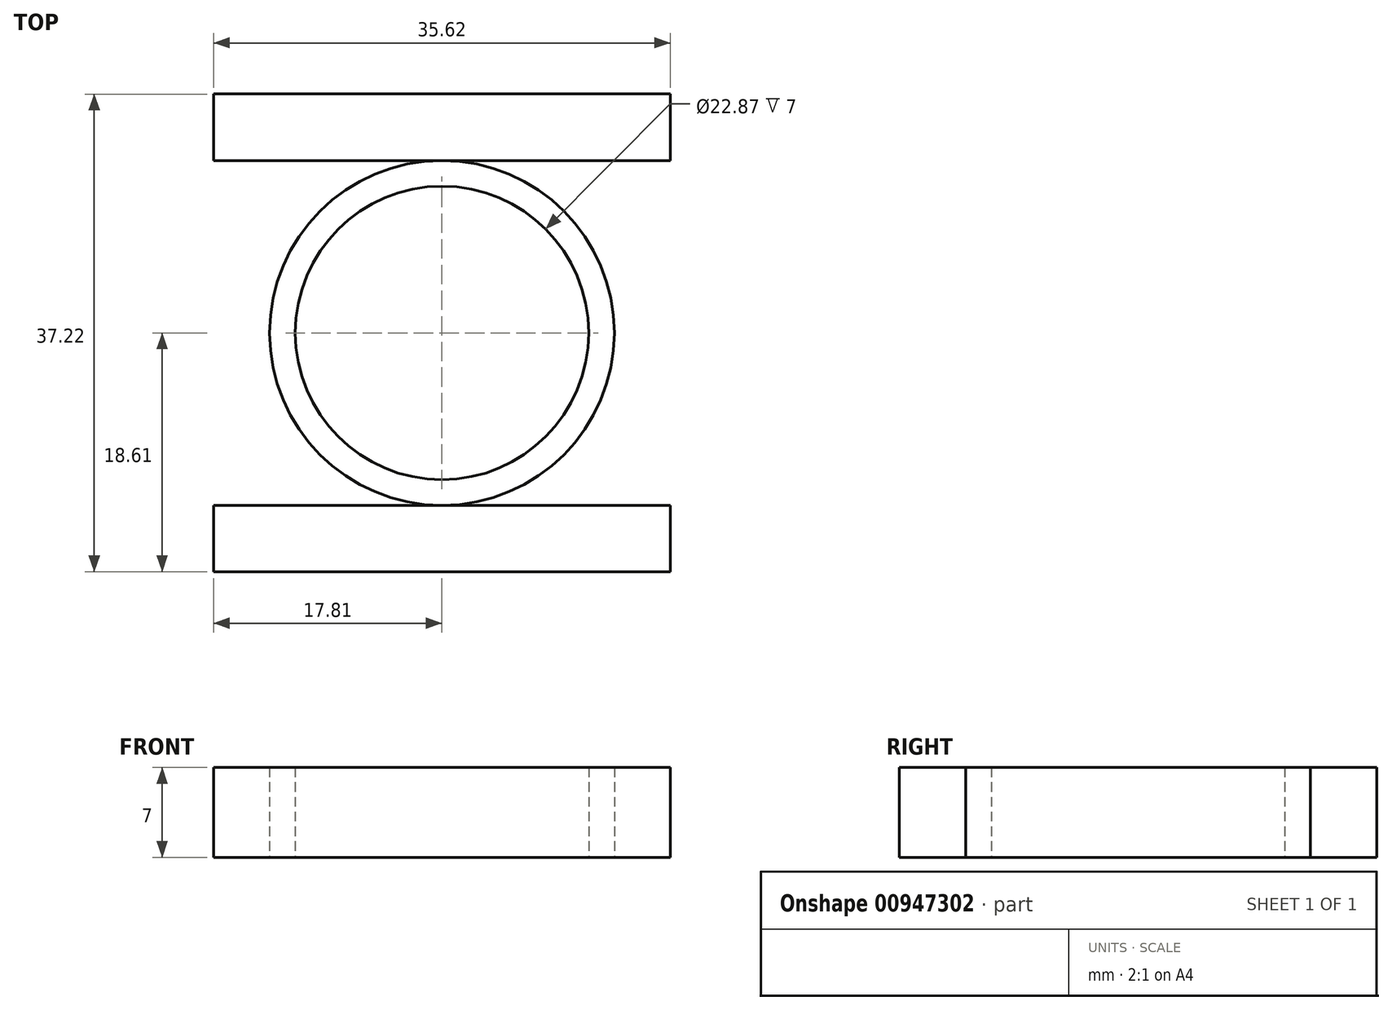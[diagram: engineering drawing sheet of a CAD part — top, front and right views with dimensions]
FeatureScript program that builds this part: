
annotation { "Feature Type Name" : "Feature", "Feature Type Description" : "" }
export const myFeature = defineFeature(function(context is Context, id is Id, definition is map)
    precondition{}
    {
        {
            var Q0;
            Q0=qCreatedBy(makeId("Top.planeOp"),FACE);
            var sketch = newSketch(context, id + "F0", { "sketchPlane" : qUnion([Q0])});
            skCircle(sketch, "E0", {"center": v(0, 0) * mm, "radius": 11.43 * mm});
            skCircle(sketch, "E1.0", {"center": v(0, 0) * mm, "radius": 13.43 * mm});
            skLineSegment(sketch, "E2.bottom", {"start": v(0, 18.61) * mm, "end": v(-17.81, 18.61) * mm});
            skLineSegment(sketch, "E2.top", {"start": v(0, 13.43) * mm, "end": v(-17.81, 13.43) * mm});
            skLineSegment(sketch, "E2.left", {"start": v(0, 18.61) * mm, "end": v(0, 13.43) * mm});
            skLineSegment(sketch, "E2.right", {"start": v(-17.81, 18.61) * mm, "end": v(-17.81, 13.43) * mm});
            skLineSegment(sketch, "E3.bottom", {"start": v(0, 18.61) * mm, "end": v(17.8, 18.61) * mm});
            skLineSegment(sketch, "E3.top", {"start": v(0, 13.43) * mm, "end": v(17.8, 13.43) * mm});
            skLineSegment(sketch, "E3.right", {"start": v(17.8, 18.61) * mm, "end": v(17.8, 13.43) * mm});
            skLineSegment(sketch, "E4.MirrorCS", {"start": v(0, -18.61) * mm, "end": v(17.8, -18.61) * mm});
            skLineSegment(sketch, "E5.MirrorCS", {"start": v(17.8, -18.61) * mm, "end": v(17.8, -13.43) * mm});
            skLineSegment(sketch, "E6.MirrorCS", {"start": v(0, -13.43) * mm, "end": v(17.8, -13.43) * mm});
            skLineSegment(sketch, "E7.MirrorCS", {"start": v(0, -18.61) * mm, "end": v(-17.81, -18.61) * mm});
            skLineSegment(sketch, "E8.MirrorCS", {"start": v(0, -13.43) * mm, "end": v(-17.81, -13.43) * mm});
            skLineSegment(sketch, "E9.MirrorCS", {"start": v(-17.81, -18.61) * mm, "end": v(-17.81, -13.43) * mm});
            skSolve(sketch);
        }
        {
            var Q0;
            Q0 = qSketchRegion(id + "F0", true);
            extrude(context, id + "F1", {"entities" : qUnion([Q0]), "depth" : 7 * mm, "offsetDistance" : 25 * mm});
        }
    });
